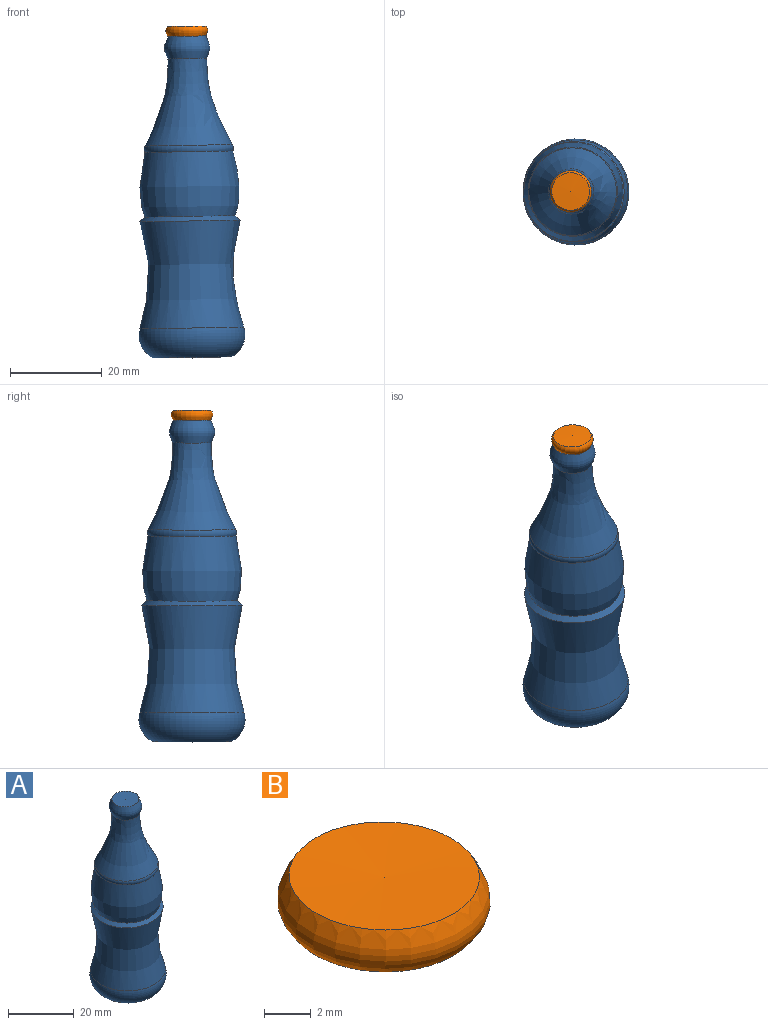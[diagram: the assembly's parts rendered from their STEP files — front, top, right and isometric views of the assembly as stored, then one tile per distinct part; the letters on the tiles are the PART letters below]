
ASSEMBLY  parts=2 mates=1
PART A: 9 faces, bbox 25.1x25.1x70.9 mm
  f0: cone r=4.12mm half-angle=89deg, axis (-0.02,0,1), area 53.4mm2, adj f1
  f1: revolved ~9.92x9.92mm, area 151.4mm2, adj f0,f2
  f2: revolved ~19.15x19.14mm, area 752.9mm2, adj f1,f3
  f3: torus R=8.18mm, axis (-0.02,0,1), area 88.1mm2, adj f2,f4
  f4: revolved ~21.66x21.66mm, area 944.2mm2, adj f3,f5
  f5: cone r=9.84mm half-angle=48.3deg, axis (0.02,0,-1), area 97.8mm2, adj f4,f6
  f6: revolved ~23.76x22.71mm, area 1480.1mm2, adj f5,f7
  f7: torus R=6.17mm, axis (-0.02,0,1), area 511mm2, adj f6,f8
  f8: cone r=8.63mm half-angle=89deg, axis (-0.02,0,1), area 234.1mm2, adj f7
PART B: 3 faces, bbox 9.1x9.1x2.3 mm
  f0: revolved ~9.14x9.14mm, area 66.4mm2, adj f1,f2
  f1: cone r=4.12mm half-angle=89deg, axis (0.02,0,1), area 53.4mm2, adj f0
  f2: cone r=4.08mm half-angle=89deg, axis (0.02,0,1), area 52.4mm2, adj f0
PLACE A t=(2.34,-8.51,-15.06)mm fixed
PLACE B rot(axis=(-1,0,0),180deg) t=(2.34,-8.51,33.71)mm
MATE cylindrical A.f5 <-> B.f2  axis (-0.02,0,1) through (-25.57,-8.51,8.17)mm
